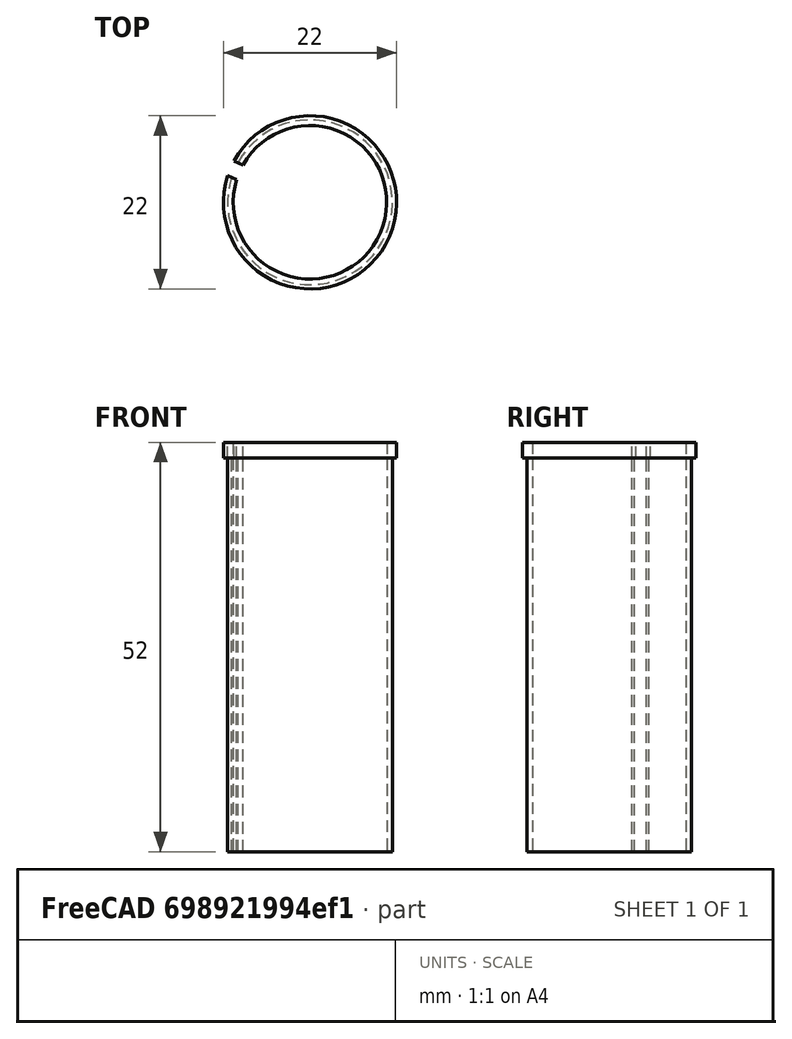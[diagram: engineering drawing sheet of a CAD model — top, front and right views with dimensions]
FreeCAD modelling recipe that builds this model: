
FCSTD DOCUMENT  (FreeCAD 0.16R)
Label: SeatSpacer
License: All rights reserved
LicenseURL: http://en.wikipedia.org/wiki/All_rights_reserved
objects: Sketcher::SketchObject×2, PartDesign::Pad×2, Mesh::Feature×1
note: 6 computed .brp shape members not serialized (recipe doc carries the construction recipe); baked Part::Feature solids carry a one-line shape summary decoded from their .brp

FEATURE [Sketcher::SketchObject] Sketch
  sketch-geometry (4):
    g0: ArcOfCircle CenterX=0 CenterY=0 CenterZ=0 NormalX=0 NormalY=0 NormalZ=1 Radius=9.75 StartAngle=2.83713 EndAngle=8.91483
    g1: ArcOfCircle CenterX=0 CenterY=0 CenterZ=0 NormalX=0 NormalY=0 NormalZ=1 Radius=10.465 StartAngle=2.83009 EndAngle=8.92187
    g2: LineSegment StartX=-9.16927 StartY=5.04388 StartZ=0 EndX=-8.50949 EndY=4.75932 EndZ=0
    g3: LineSegment StartX=-9.30158 StartY=2.92286 StartZ=0 EndX=-9.96136 EndY=3.20742 EndZ=0
  constraints (11):
    c: Coincident(g0,g-1)
    c: Coincident(g1,g-1)
    c: Radius(g1) = 10.465
    c: Radius(g0) = 9.75
    c: Coincident(g0,g2)
    c: Coincident(g2,g1)
    c: Coincident(g3,g0)
    c: Coincident(g3,g1)
    c: Parallel(g2,g3)
    c: Distance(g1,g1) = 2
    c: Distance(g0,g0) = 2
FEATURE [PartDesign::Pad] Pad  label="spacer"
  Length = 50
  Length2 = 100
  Sketch = -> Sketch
  Type = 0
FEATURE [Sketcher::SketchObject] Sketch001
  ExternalGeometry = -> [Pad]
  Placement = pos=(0,0,50) rot=(0,0,1;0rad)
  Support = -> Pad [Face6]
  sketch-geometry (4):
    g0: ArcOfCircle CenterX=0 CenterY=0 CenterZ=0 NormalX=0 NormalY=0 NormalZ=1 Radius=11 StartAngle=2.82542 EndAngle=8.92654
    g1: ArcOfCircle CenterX=0 CenterY=0 CenterZ=0 NormalX=0 NormalY=0 NormalZ=1 Radius=9.75 StartAngle=2.83713 EndAngle=8.91483
    g2: LineSegment StartX=-8.50949 StartY=4.75932 StartZ=0 EndX=-9.66268 EndY=5.25668 EndZ=0
    g3: LineSegment StartX=-9.30158 StartY=2.92286 StartZ=0 EndX=-10.4548 EndY=3.42022 EndZ=0
  constraints (11):
    c: Radius(g0) = 11
    c: Coincident(g0,g-1)
    c: Coincident(g1,g-3)
    c: Coincident(g1,g-6)
    c: Radius(g1) = 9.75
    c: Coincident(g0,g3)
    c: Coincident(g2,g0)
    c: Parallel(g3,g-8)
    c: Parallel(g2,g-7)
    c: Coincident(g2,g1)
    c: Coincident(g3,g1)
FEATURE [PartDesign::Pad] Pad001
  Length = 2
  Length2 = 100
  Sketch = -> Sketch001
  Type = 0
FEATURE [Mesh::Feature] Mesh  label="Pad001 (Meshed)"
